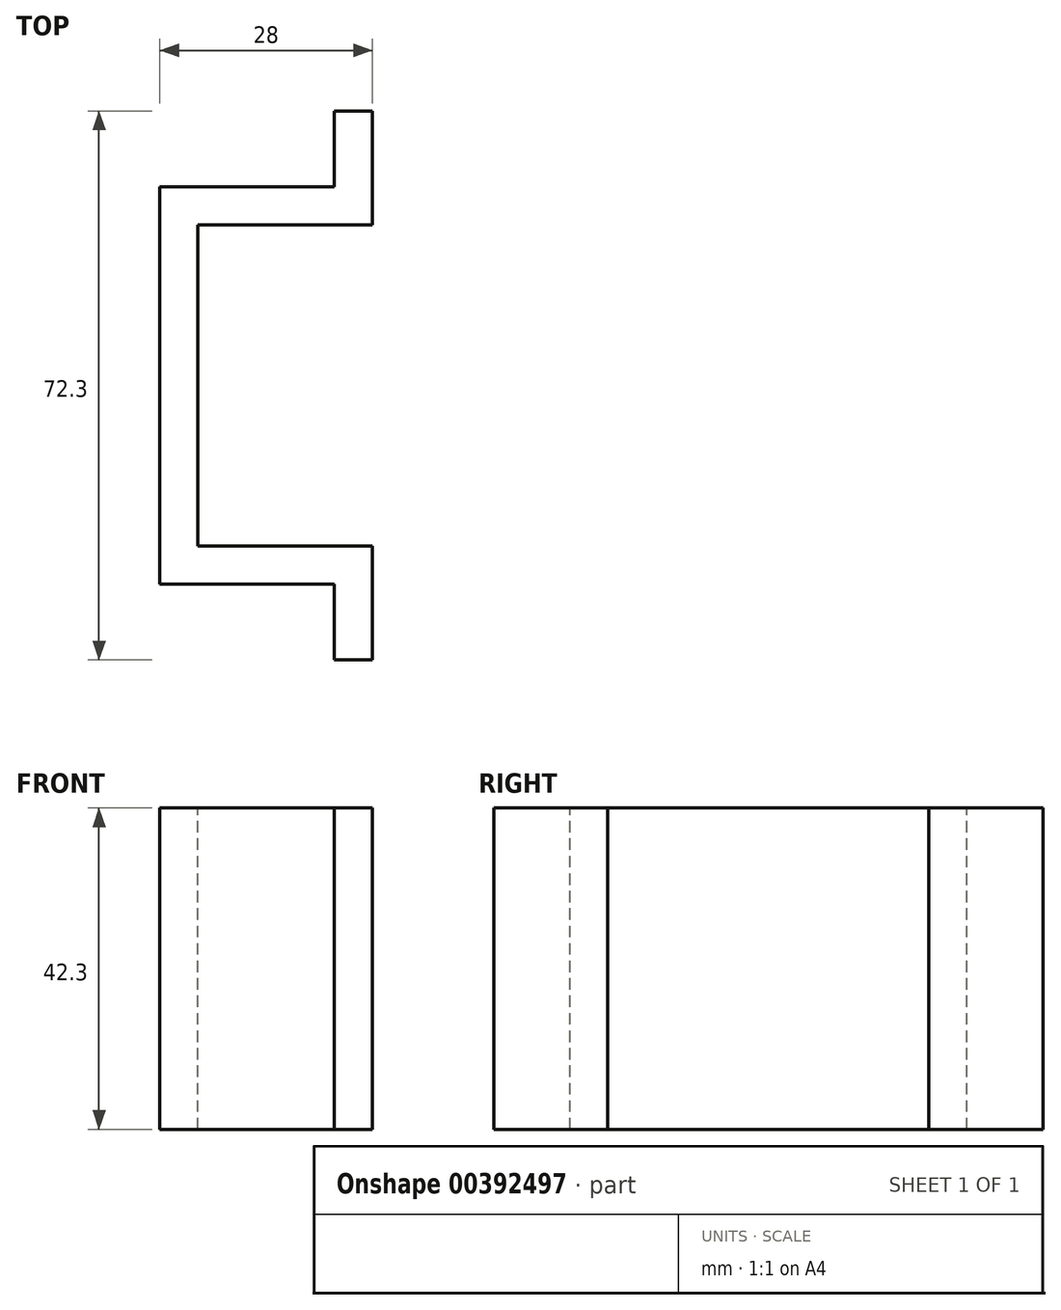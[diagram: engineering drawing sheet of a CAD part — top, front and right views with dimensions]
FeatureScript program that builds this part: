
annotation { "Feature Type Name" : "Feature", "Feature Type Description" : "" }
export const myFeature = defineFeature(function(context is Context, id is Id, definition is map)
    precondition{}
    {
        {
            var Q0;
            Q0=qCreatedBy(makeId("Top.planeOp"),FACE);
            var sketch = newSketch(context, id + "F0", { "sketchPlane" : qUnion([Q0])});
            skLineSegment(sketch, "E0", {"start": v(0, 0) * mm, "end": v(0, 44.23) * mm, "construction": true});
            skLineSegment(sketch, "E1.bottom", {"start": v(-2.5, 40.19) * mm, "end": v(-17.5, 40.19) * mm, "construction": true});
            skLineSegment(sketch, "E1.top", {"start": v(-2.5, -40.19) * mm, "end": v(-17.5, -40.19) * mm, "construction": true});
            skLineSegment(sketch, "E1.left", {"start": v(-2.5, 40.19) * mm, "end": v(-2.5, -40.19) * mm, "construction": true});
            skLineSegment(sketch, "E1.right", {"start": v(-17.5, 40.19) * mm, "end": v(-17.5, -40.19) * mm, "construction": true});
            skPoint(sketch, "E1.middle", {"position": v(-10, 0) * mm});
            skLineSegment(sketch, "E2", {"start": v(-23, 0) * mm, "end": v(-23, 21.15) * mm});
            skLineSegment(sketch, "E3", {"start": v(-28, 0) * mm, "end": v(-28, 26.15) * mm});
            skLineSegment(sketch, "E4", {"start": v(-23, 21.15) * mm, "end": v(0, 21.15) * mm});
            skLineSegment(sketch, "E5", {"start": v(0, 0) * mm, "end": v(-49.21, 0) * mm, "construction": true});
            skLineSegment(sketch, "E6", {"start": v(-28, 26.15) * mm, "end": v(-5, 26.15) * mm});
            skLineSegment(sketch, "E7", {"start": v(-5, 26.15) * mm, "end": v(-5, 36.15) * mm});
            skLineSegment(sketch, "E8", {"start": v(-5, 36.15) * mm, "end": v(0, 36.15) * mm});
            skLineSegment(sketch, "E9", {"start": v(0, 36.15) * mm, "end": v(0, 21.15) * mm});
            skLineSegment(sketch, "E10.MirrorCS", {"start": v(0, 0) * mm, "end": v(0, -44.23) * mm, "construction": true});
            skLineSegment(sketch, "E11.MirrorCS", {"start": v(0, -36.15) * mm, "end": v(0, -21.15) * mm});
            skLineSegment(sketch, "E12.MirrorCS", {"start": v(-23, 0) * mm, "end": v(-23, -21.15) * mm});
            skLineSegment(sketch, "E13.MirrorCS", {"start": v(-28, 0) * mm, "end": v(-28, -26.15) * mm});
            skLineSegment(sketch, "E14.MirrorCS", {"start": v(-5, -36.15) * mm, "end": v(0, -36.15) * mm});
            skLineSegment(sketch, "E15.MirrorCS", {"start": v(-5, -26.15) * mm, "end": v(-5, -36.15) * mm});
            skLineSegment(sketch, "E16.MirrorCS", {"start": v(-28, -26.15) * mm, "end": v(-5, -26.15) * mm});
            skLineSegment(sketch, "E17.MirrorCS", {"start": v(-23, -21.15) * mm, "end": v(0, -21.15) * mm});
            skSolve(sketch);
        }
        {
            var Q0;
            Q0=makeQuery(id+"F0.imprint","IMPRINT",FACE,{"disambiguationData":[TD([[makeQuery(id+"F0.imprint","IMPRINT",EDGE,{"derivedFrom":sQuery(id+"F0.wireOp",EDGE,"E2")}),1.0]])]});
            extrude(context, id + "F1", {"entities" : qUnion([Q0]), "endBound" : BoundingType.SYMMETRIC, "oppositeDirection" : true, "depth" : 42.3 * mm});
        }
    });
